# Revit family: Flanschmutter
name_source: partatom
category: HLS-Bauteile
revit_build: Autodesk Revit 2017 (Build: 20190507_1515(x64)
units: mm (PartAtom-declared; Revit-internal decimal feet)

## family parameters
Arbeitsebenenbasiert = Ja
Beim Laden mit Abzugskörper schneiden = Nein
Bemaßung runder Anschluss = Durchmesser verwenden
Gemeinsam genutzt = Ja
Immer vertikal = Nein
Raumberechnungspunkt = Nein
Teiletyp = Normal

## types (4) — shared parameters
Fabrikat = MEFA
Firma = MEFA Befestigungs- und Montagesysteme GmbH
Kurztext1 = Flanschmutter
Material = Stahl
Mengeneinheit = St
Oberflaeche = galvanisch verzinkt
Vorgabe-Ansicht = 1219 mm

## per-type parameters (varying)
| type | Artikelnummer | B | C | Durchmesser Flansch | EAN | F2 | Gewicht | Gewicht pro Bauteil | Gewinde | H | Höhe | Kurztext2 | Lochung | Schlüsselweite | vpe |
| Flanschmutter M16 | 0470016 | 17 mm | 6 mm  [stored 0.019685 ft] | 34,5 mm | 4250928457585 | 12 mm  [stored 0.0393701 ft] | 0.05 kg | 0.05 kg | M16 | 16 mm  [stored 0.0524934 ft] | 16 mm | M16 SW 24 | 7 mm  [stored 0.0229659 ft] | 24 | 25 St |
| Flanschmutter M10 | 0470020 | 11 mm  [stored 0.0360892 ft] | 6 mm  [stored 0.019685 ft] | 21,8 mm | 4250928457561 | 8 mm  [stored 0.0262467 ft] | 0.01 kg | 0.01 kg | M10 | 10 mm  [stored 0.0328084 ft] | 10 mm | M10 SW 15 | 4 mm  [stored 0.0131234 ft] | 15 | 25 St |
| Flanschmutter M12 | 0470022 | 13 mm | 6 mm  [stored 0.019685 ft] | 26 mm | 4250928457578 | 9 mm  [stored 0.0295276 ft] | 0.02 kg | 0.02 kg | M12 | 12 mm  [stored 0.0393701 ft] | 12 mm | M12 SW 18 | 5 mm  [stored 0.0164042 ft] | 18 | 25 St |
| Flanschmutter M 8 | 0470008 | 9 mm  [stored 0.0295276 ft] | 5 mm  [stored 0.0164042 ft] | 17,9 mm | 4250928457554 | 7 mm  [stored 0.0229659 ft] | 0.01 kg | 0.01 kg | M8 | 8 mm  [stored 0.0262467 ft] | 8 mm | M8 SW 13 | 3 mm  [stored 0.00984252 ft] | 13 | 50 St |

note: [stored X ft] marks values corroborated as IEEE doubles in the binary element streams (Revit-internal decimal feet)

## geometry (parser evidence)
native form markers: Sweep x3
no freeform markers — native parametric forms only
